# Revit family: ADB Electric fryers cupboard 400
name_source: partatom
category: Equipement spécialisé
units: mm (PartAtom-declared; Revit-internal decimal feet)

## family parameters
Basée sur le plan de construction = Non
Conserver l'orientation des annotations = Non
Cote de connecteur circulaire = Utiliser le diamètre
Couper avec des vides une fois chargée = Non
Numéro OmniClass = 23.40.40.14.17.11
Partagée = Non
Repère de localisation dans la pièce = Non
Titre OmniClass = Cookers, Ovens, Stoves
Toujours verticalement = Oui
Type d'élément = Normal

## types (6) — shared parameters
Commentaires du type = Ambassade range - Cupboards - Electric fryers
Fabricant = Société Industrielle de Lacanche
URL = https://www.ambassade-de-bourgogne.com
URL Cutsheet = https://www.ambassade-de-bourgogne.com
zero-valued in all types: Elévation par défaut

## per-type parameters (varying)
| type | C | Cuve et bloc | D | Description | Electric power | Height | Number of Poles | Operational Current | Phase | Poids base |
| CME 434 FRI | 300 mm | Friteuse : Poignée courbe | 755 mm  [stored 2.47703 ft] | Cupboard Electric fryers 12l - 12kW | 12000 W | 1017 mm  [stored 3.33661 ft] | 3 | 17 A | 3 | 50.00 kg |
| CME 419 FRI | 300 mm | Friteuse : Poignée courbe | 755 mm  [stored 2.47703 ft] | Cupboard Electric fryers 9l - 9kW | 9000 W | 1017 mm  [stored 3.33661 ft] | 3 | 13 A | 3 | 49.00 kg |
| CME 418 FRI | 300 mm | Friteuse : Poignée droite | 755 mm  [stored 2.47703 ft] | Cupboard Electric fryers 8l - 8kW | 8000 W | 1017 mm  [stored 3.33661 ft] | 1 | 12 A | 1 | 49.00 kg |
| CME 416 FR | 200 mm  [stored 0.656168 ft] | Friteuse : Poignée droite | 760 mm | cupboard Electric fryers 6l - 6kW | 6000 W | 1012 mm  [stored 3.32021 ft] | 3 | 9 A | 3 | 48.00 kg |
| CME 415 FR | 200 mm  [stored 0.656168 ft] | Friteuse : Poignée droite | 760 mm | Cupboard Electric fryers 6l -4,5kW | 4500 W | 1012 mm  [stored 3.32021 ft] | 3 | 7 A | 3 | 48.00 kg |
| CME 413 FR | 200 mm  [stored 0.656168 ft] | Friteuse : Poignée droite | 760 mm | Cupboard Electric fryers 6l -3kW | 3000 W | 1012 mm  [stored 3.32021 ft] | 1 | 13 A | 1 | 48.00 kg |

note: column(s) folded — value = type name in every type: Modèle

note: [stored X ft] marks values corroborated as IEEE doubles in the binary element streams (Revit-internal decimal feet)
